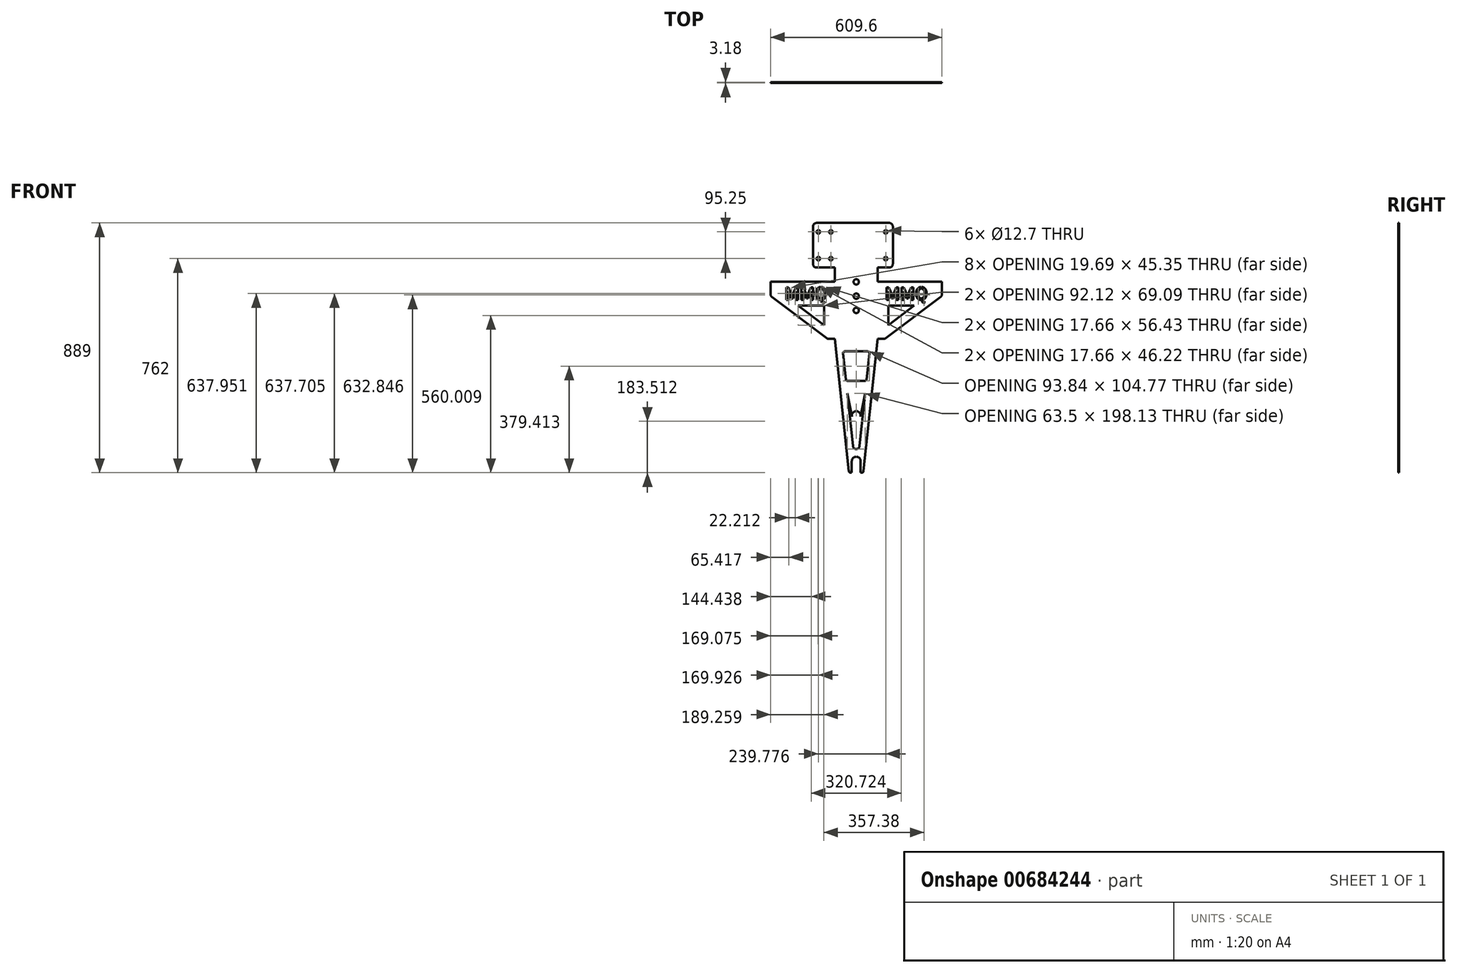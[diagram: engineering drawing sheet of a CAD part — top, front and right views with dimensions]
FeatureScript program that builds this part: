
annotation { "Feature Type Name" : "Feature", "Feature Type Description" : "" }
export const myFeature = defineFeature(function(context is Context, id is Id, definition is map)
    precondition{}
    {
        {
            var Q0;
            Q0=qCreatedBy(makeId("Front.planeOp"),FACE);
            var sketch = newSketch(context, id + "F0", { "sketchPlane" : qUnion([Q0])});
            skLineSegment(sketch, "E0.bottom", {"start": v(-97.37, -101.6) * mm, "end": v(-76.2, -101.6) * mm});
            skLineSegment(sketch, "E0.top", {"start": v(-304.8, 101.6) * mm, "end": v(-76.2, 101.6) * mm});
            skLineSegment(sketch, "E0.left", {"start": v(-304.8, 57.15) * mm, "end": v(-304.8, 101.6) * mm});
            skLineSegment(sketch, "E0.right", {"start": v(304.8, 57.15) * mm, "end": v(304.8, 101.6) * mm});
            skPoint(sketch, "E0.middle", {"position": v(0, 0) * mm});
            skLineSegment(sketch, "E1", {"start": v(-15.88, -577.85) * mm, "end": v(-19.7, -577.85) * mm});
            skLineSegment(sketch, "E2", {"start": v(15.87, -577.85) * mm, "end": v(19.7, -577.85) * mm});
            skPoint(sketch, "E3", {"position": v(-76.2, -101.6) * mm});
            skPoint(sketch, "E4", {"position": v(76.2, -101.6) * mm});
            skLineSegment(sketch, "E5", {"start": v(-76.2, -101.6) * mm, "end": v(-26, -572.17) * mm});
            skLineSegment(sketch, "E6", {"start": v(76.2, -101.6) * mm, "end": v(26, -572.17) * mm});
            skPoint(sketch, "E7", {"position": v(0, -295.28) * mm});
            skPoint(sketch, "E8", {"position": v(0, -523.88) * mm});
            skPoint(sketch, "E9", {"position": v(-31.75, -295.28) * mm});
            skPoint(sketch, "E10", {"position": v(31.75, -295.28) * mm});
            skLineSegment(sketch, "E11", {"start": v(-31.75, -295.28) * mm, "end": v(31.75, -295.28) * mm});
            skArc(sketch, "E12", {"start": v(15.58, -377.7) * mm, "mid": v(0, -358.78) * mm, "end": v(-15.58, -377.7) * mm});
            skLineSegment(sketch, "E13", {"start": v(-31.75, -295.28) * mm, "end": v(-15.58, -377.7) * mm});
            skLineSegment(sketch, "E14", {"start": v(31.75, -295.28) * mm, "end": v(15.58, -377.7) * mm});
            skLineSegment(sketch, "E15", {"start": v(-31.75, -295.28) * mm, "end": v(-11.88, -481.52) * mm});
            skLineSegment(sketch, "E16", {"start": v(31.75, -295.28) * mm, "end": v(11.88, -481.52) * mm});
            skArc(sketch, "E17", {"start": v(-11.88, -481.52) * mm, "mid": v(0, -493.4) * mm, "end": v(11.88, -481.52) * mm});
            skLineSegment(sketch, "E18", {"start": v(-76.2, 101.6) * mm, "end": v(-76.2, 152.4) * mm});
            skPoint(sketch, "E18.startSnap0", {"position": v(0, 101.6) * mm});
            skLineSegment(sketch, "E19", {"start": v(76.2, 101.6) * mm, "end": v(76.2, 152.4) * mm});
            skLineSegment(sketch, "E20", {"start": v(-76.2, 152.4) * mm, "end": v(-141.22, 152.4) * mm});
            skLineSegment(sketch, "E21", {"start": v(76.2, 152.4) * mm, "end": v(117.6, 152.4) * mm});
            skPoint(sketch, "E22.orphan", {"position": v(-141.22, 361.95) * mm});
            skPoint(sketch, "E23.orphan", {"position": v(117.6, 361.95) * mm});
            skLineSegment(sketch, "E24", {"start": v(-153.92, 298.45) * mm, "end": v(-153.92, 165.1) * mm});
            skPoint(sketch, "E24.endSnap0", {"position": v(-108.71, 152.4) * mm});
            skLineSegment(sketch, "E25", {"start": v(130.3, 298.45) * mm, "end": v(130.3, 165.1) * mm});
            skLineSegment(sketch, "E26", {"start": v(-141.22, 152.4) * mm, "end": v(-141.22, 152.4) * mm});
            skLineSegment(sketch, "E27", {"start": v(117.6, 152.4) * mm, "end": v(117.6, 152.4) * mm});
            skPoint(sketch, "E28.end.orphan", {"position": v(-141.22, 317.6) * mm});
            skPoint(sketch, "E29.start.orphan", {"position": v(117.6, 317.5) * mm});
            skPoint(sketch, "E30.start.orphan", {"position": v(-15.88, -539.75) * mm});
            skPoint(sketch, "E31.start.orphan", {"position": v(15.87, -539.75) * mm});
            skPoint(sketch, "E32.center.orphan", {"position": v(0, -552.44) * mm});
            skArc(sketch, "E33", {"start": v(15.88, -536.58) * mm, "mid": v(0, -520.7) * mm, "end": v(-15.87, -536.58) * mm});
            skLineSegment(sketch, "E34", {"start": v(15.87, -577.85) * mm, "end": v(15.87, -536.58) * mm});
            skLineSegment(sketch, "E35", {"start": v(-15.88, -577.85) * mm, "end": v(-15.88, -536.58) * mm});
            skPoint(sketch, "E36", {"position": v(0, -520.7) * mm});
            skLineSegment(sketch, "E37", {"start": v(-299.72, 46.99) * mm, "end": v(-104.99, -99.06) * mm});
            skLineSegment(sketch, "E38", {"start": v(299.72, 46.99) * mm, "end": v(104.99, -99.06) * mm});
            skPoint(sketch, "E39.orphan", {"position": v(-304.8, -101.6) * mm});
            skPoint(sketch, "E40.orphan", {"position": v(304.8, -101.6) * mm});
            skLineSegment(sketch, "E41.trimOffspring", {"start": v(76.2, 101.6) * mm, "end": v(304.8, 101.6) * mm});
            skLineSegment(sketch, "E42.trimOffspring", {"start": v(76.2, -101.6) * mm, "end": v(97.37, -101.6) * mm});
            skCircle(sketch, "E43", {"center": v(104.9, 279.4) * mm, "radius": 6.35 * mm});
            skCircle(sketch, "E44", {"center": v(104.9, 184.15) * mm, "radius": 6.35 * mm});
            skCircle(sketch, "E45", {"center": v(-90.42, 184.15) * mm, "radius": 6.35 * mm});
            skCircle(sketch, "E46", {"center": v(-90.42, 279.4) * mm, "radius": 6.35 * mm});
            skPoint(sketch, "E47", {"position": v(0, 184.15) * mm});
            skPoint(sketch, "E48", {"position": v(0, 279.4) * mm});
            skLineSegment(sketch, "E49", {"start": v(-141.22, 311.15) * mm, "end": v(117.6, 311.15) * mm});
            skPoint(sketch, "E50.end.orphan", {"position": v(130.3, 317.5) * mm});
            skPoint(sketch, "E51.orphan", {"position": v(-153.92, 317.6) * mm});
            skLineSegment(sketch, "E52", {"start": v(-115.82, 285.75) * mm, "end": v(-115.82, 177.8) * mm});
            skCircle(sketch, "E53", {"center": v(-134.87, 184.15) * mm, "radius": 6.35 * mm});
            skCircle(sketch, "E54", {"center": v(-134.87, 279.4) * mm, "radius": 6.35 * mm});
            skPoint(sketch, "E55", {"position": v(-115.82, 285.75) * mm});
            skPoint(sketch, "E56", {"position": v(-115.82, 177.8) * mm});
            skPoint(sketch, "E57.orphan", {"position": v(-115.82, 311.15) * mm});
            skPoint(sketch, "E58.orphan", {"position": v(-115.82, 152.4) * mm});
            skPoint(sketch, "E59.orphan", {"position": v(0, -101.6) * mm});
            skPoint(sketch, "E60.trimOffspring.end.orphan", {"position": v(0, -539.75) * mm});
            skCircle(sketch, "E61", {"center": v(0, 101.6) * mm, "radius": 9.52 * mm});
            skCircle(sketch, "E62", {"center": v(0, 50.8) * mm, "radius": 9.52 * mm});
            skText(sketch, "E63", { "text": "MMQ", "fontName": "AllertaStencil-Regular.ttf"});
            skText(sketch, "E64", { "text": "MMQ", "fontName": "AllertaStencil-Regular.ttf"});
            skPoint(sketch, "E65.visualSharp", {"position": v(-153.92, 311.15) * mm});
            skArc(sketch, "E65.filletArc", {"start": v(-141.22, 311.15) * mm, "mid": v(-150.2, 307.43) * mm, "end": v(-153.92, 298.45) * mm});
            skPoint(sketch, "E66.visualSharp", {"position": v(-153.92, 152.4) * mm});
            skArc(sketch, "E66.filletArc", {"start": v(-153.92, 165.1) * mm, "mid": v(-150.2, 156.12) * mm, "end": v(-141.22, 152.4) * mm});
            skPoint(sketch, "E67.visualSharp", {"position": v(130.3, 311.15) * mm});
            skArc(sketch, "E67.filletArc", {"start": v(130.3, 298.45) * mm, "mid": v(126.58, 307.43) * mm, "end": v(117.6, 311.15) * mm});
            skPoint(sketch, "E68.visualSharp", {"position": v(130.3, 152.4) * mm});
            skArc(sketch, "E68.filletArc", {"start": v(117.6, 152.4) * mm, "mid": v(126.58, 156.12) * mm, "end": v(130.3, 165.1) * mm});
            skPoint(sketch, "E69.visualSharp", {"position": v(-304.8, 50.8) * mm});
            skArc(sketch, "E69.filletArc", {"start": v(-304.8, 57.15) * mm, "mid": v(-303.46, 51.47) * mm, "end": v(-299.72, 46.99) * mm});
            skPoint(sketch, "E70.visualSharp", {"position": v(-101.6, -101.6) * mm});
            skArc(sketch, "E70.filletArc", {"start": v(-104.99, -99.06) * mm, "mid": v(-101.38, -100.95) * mm, "end": v(-97.37, -101.6) * mm});
            skPoint(sketch, "E71.visualSharp", {"position": v(101.6, -101.6) * mm});
            skArc(sketch, "E71.filletArc", {"start": v(97.37, -101.6) * mm, "mid": v(101.38, -100.95) * mm, "end": v(104.99, -99.06) * mm});
            skPoint(sketch, "E72.visualSharp", {"position": v(304.8, 50.8) * mm});
            skArc(sketch, "E72.filletArc", {"start": v(299.72, 46.99) * mm, "mid": v(303.46, 51.47) * mm, "end": v(304.8, 57.15) * mm});
            skPoint(sketch, "E73.visualSharp", {"position": v(-25.4, -577.85) * mm});
            skArc(sketch, "E73.filletArc", {"start": v(-26, -572.17) * mm, "mid": v(-23.94, -576.22) * mm, "end": v(-19.7, -577.85) * mm});
            skPoint(sketch, "E74.visualSharp", {"position": v(25.4, -577.85) * mm});
            skArc(sketch, "E74.filletArc", {"start": v(19.7, -577.85) * mm, "mid": v(23.94, -576.22) * mm, "end": v(26, -572.17) * mm});
            skLineSegment(sketch, "E75", {"start": v(-37.1, -245.15) * mm, "end": v(-46.92, -153.07) * mm});
            skLineSegment(sketch, "E76", {"start": v(37.1, -245.15) * mm, "end": v(46.92, -153.07) * mm});
            skLineSegment(sketch, "E77", {"start": v(40.6, -146.05) * mm, "end": v(-40.6, -146.05) * mm});
            skLineSegment(sketch, "E78", {"start": v(-30.78, -250.83) * mm, "end": v(30.78, -250.83) * mm});
            skPoint(sketch, "E79.visualSharp", {"position": v(-47.67, -146.05) * mm});
            skArc(sketch, "E79.filletArc", {"start": v(-40.6, -146.05) * mm, "mid": v(-45.33, -148.15) * mm, "end": v(-46.92, -153.07) * mm});
            skPoint(sketch, "E80.visualSharp", {"position": v(47.67, -146.05) * mm});
            skArc(sketch, "E80.filletArc", {"start": v(46.92, -153.07) * mm, "mid": v(45.33, -148.15) * mm, "end": v(40.6, -146.05) * mm});
            skPoint(sketch, "E81.visualSharp", {"position": v(36.5, -250.83) * mm});
            skArc(sketch, "E81.filletArc", {"start": v(30.78, -250.83) * mm, "mid": v(35.03, -249.2) * mm, "end": v(37.1, -245.15) * mm});
            skPoint(sketch, "E82.visualSharp", {"position": v(-36.5, -250.83) * mm});
            skArc(sketch, "E82.filletArc", {"start": v(-37.1, -245.15) * mm, "mid": v(-35.03, -249.2) * mm, "end": v(-30.78, -250.83) * mm});
            skLineSegment(sketch, "E83", {"start": v(-206.42, 16.7) * mm, "end": v(-114.3, 16.7) * mm});
            skLineSegment(sketch, "E84", {"start": v(-114.3, 16.7) * mm, "end": v(-114.3, -52.39) * mm});
            skLineSegment(sketch, "E85", {"start": v(-114.3, -52.39) * mm, "end": v(-206.42, 16.7) * mm});
            skLineSegment(sketch, "E86", {"start": v(114.3, 16.7) * mm, "end": v(114.3, -52.39) * mm});
            skLineSegment(sketch, "E87", {"start": v(114.3, -52.39) * mm, "end": v(206.42, 16.7) * mm});
            skLineSegment(sketch, "E88", {"start": v(206.42, 16.7) * mm, "end": v(114.3, 16.7) * mm});
            skPoint(sketch, "E89.center.orphan", {"position": v(0, 26.68) * mm});
            skCircle(sketch, "E90", {"center": v(0, 0) * mm, "radius": 9.53 * mm});
            const initialGuessF0  = {"E63": [-0.25489, 0.03718, 1, 0, 0.04537], "E64": [0.10249, 0.03718, 1, 0, 0.04537]};
            skSetInitialGuess(sketch, initialGuessF0);
            skSolve(sketch);
        }
        {
            var Q0;
            Q0=makeQuery(id+"F0.imprint","IMPRINT",FACE,{"disambiguationData":[TD([[makeQuery(id+"F0.imprint","IMPRINT",EDGE,{"derivedFrom":sQuery(id+"F0.wireOp",EDGE,"E0.bottom")}),1.0]])]});
            var Q1;
            Q1=makeQuery(id+"F0.imprint","IMPRINT",FACE,{"disambiguationData":[TD([[makeQuery(id+"F0.imprint","IMPRINT",EDGE,{"derivedFrom":sQuery(id+"F0.wireOp",EDGE,"E11")}),-1.0]])]});
            extrude(context, id + "F1", {"entities" : qUnion([Q0, Q1]), "depth" : 3.17 * mm, "offsetDistance" : 25.4 * mm});
        }
    });
